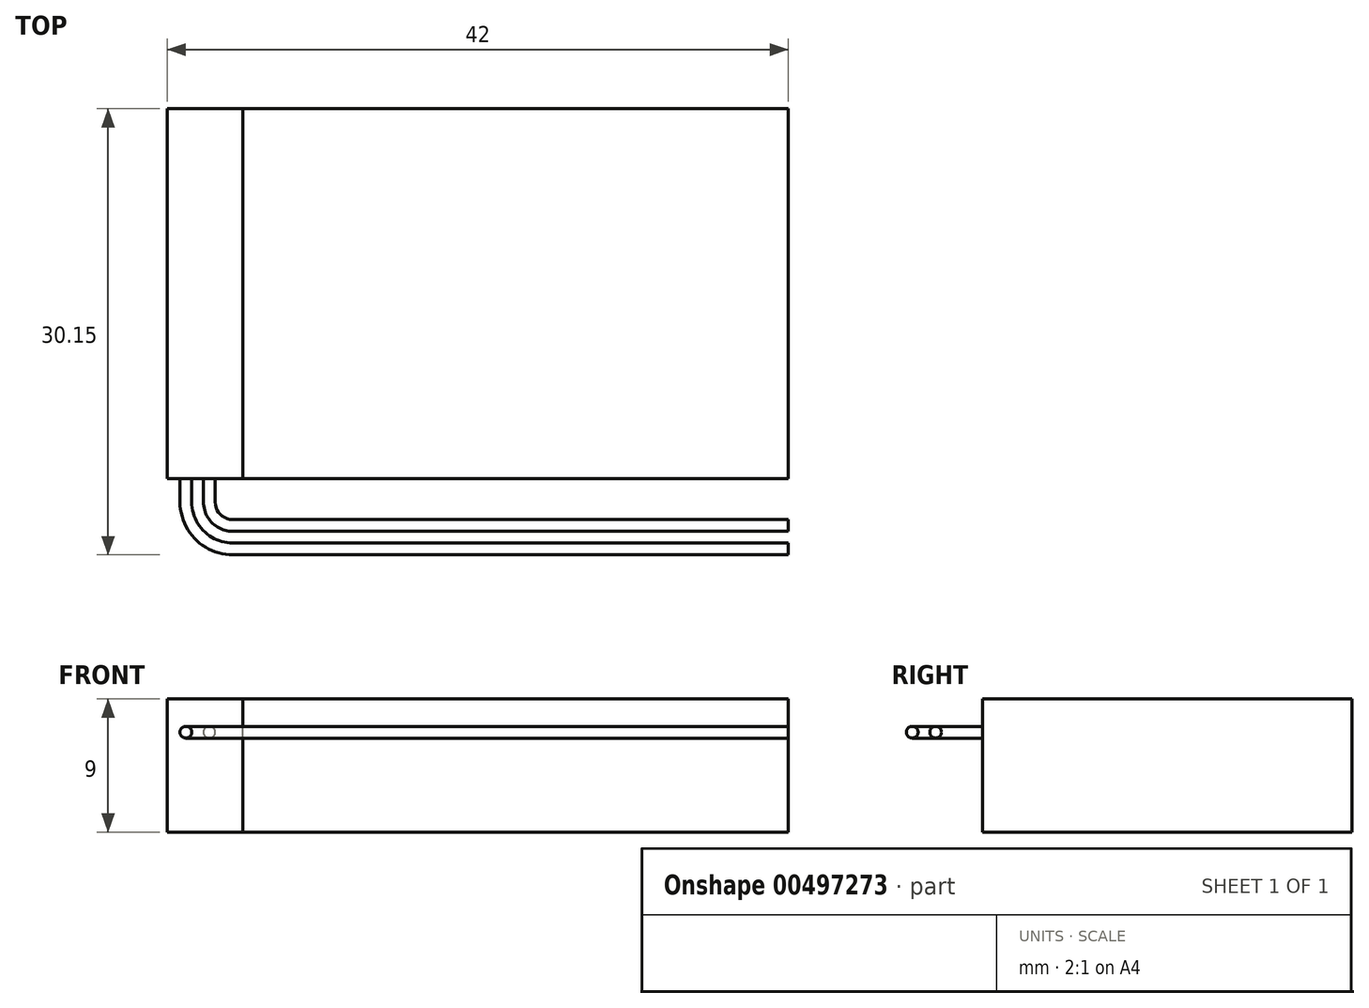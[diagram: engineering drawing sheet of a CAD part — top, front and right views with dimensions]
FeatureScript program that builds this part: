
annotation { "Feature Type Name" : "Feature", "Feature Type Description" : "" }
export const myFeature = defineFeature(function(context is Context, id is Id, definition is map)
    precondition{}
    {
        {
            var Q0;
            Q0=qCreatedBy(makeId("Top.planeOp"),FACE);
            var sketch = newSketch(context, id + "F0", { "sketchPlane" : qUnion([Q0])});
            skLineSegment(sketch, "E0.bottom", {"start": v(21, -12.5) * mm, "end": v(-21, -12.5) * mm});
            skLineSegment(sketch, "E0.top", {"start": v(21, 12.5) * mm, "end": v(-21, 12.5) * mm});
            skLineSegment(sketch, "E0.left", {"start": v(21, -12.5) * mm, "end": v(21, 12.5) * mm});
            skLineSegment(sketch, "E0.right", {"start": v(-21, -12.5) * mm, "end": v(-21, 12.5) * mm});
            skPoint(sketch, "E0.middle", {"position": v(0, 0) * mm});
            skSolve(sketch);
        }
        {
            var Q0;
            Q0=qSketchRegion(id+"F0",true);
            extrude(context, id + "F1", {"entities" : qUnion([Q0]), "depth" : 9 * mm});
        }
        {
            var Q0;
            Q0=makeQuery(id+"F1.opExtrude","CAP_FACE",FACE,{"disambiguationData":[OSD([sQuery(id+"F0.wireOp",EDGE,"E0.bottom"),sQuery(id+"F0.wireOp",EDGE,"E0.top"),sQuery(id+"F0.wireOp",EDGE,"E0.left"),sQuery(id+"F0.wireOp",EDGE,"E0.right")])],"isStart":false});
            var sketch = newSketch(context, id + "F2", { "sketchPlane" : qUnion([Q0])});
            skLineSegment(sketch, "E1.bottom", {"start": v(-21, 12.5) * mm, "end": v(-15.88, 12.5) * mm});
            skLineSegment(sketch, "E1.top", {"start": v(-21, -12.5) * mm, "end": v(-15.88, -12.5) * mm});
            skLineSegment(sketch, "E1.left", {"start": v(-21, 12.5) * mm, "end": v(-21, -12.5) * mm});
            skLineSegment(sketch, "E1.right", {"start": v(-15.88, 12.5) * mm, "end": v(-15.88, -12.5) * mm});
            skSolve(sketch);
        }
        {
            var Q0;
            Q0=makeQuery(id+"F2.imprint","IMPRINT",FACE,{"disambiguationData":[TD([[makeQuery(id+"F2.imprint","IMPRINT",EDGE,{"derivedFrom":sQuery(id+"F2.wireOp",EDGE,"E1.bottom")}),1.0]])]});
            extrude(context, id + "F3", {"entities" : qUnion([Q0]), "operationType" : NewBodyOperationType.REMOVE, "endBound" : BoundingType.THROUGH_ALL, "oppositeDirection" : true, "depth" : 9 * mm});
        }
        {
            var Q0;
            Q0=qSketchRegion(id+"F2",true);
            extrude(context, id + "F4", {"entities" : qUnion([Q0]), "oppositeDirection" : true, "depth" : 9 * mm});
        }
        {
            var Q0;
            Q0=qCreatedBy(makeId("Top.planeOp"),FACE);
            cPlane(context, id + "F5", {"entities" : qUnion([Q0]), "cplaneType" : CPlaneType.OFFSET, "offset" : .9 / 4 * 30 * mm, "width" : 152.4 * mm, "height" : 152.4 * mm});
        }
        {
            var Q0;
            Q0=makeQuery(id+"F4.opExtrude","SWEPT_FACE",FACE,{"disambiguationData":[OSD([sQuery(id+"F2.wireOp",EDGE,"E1.top")])]});
            var sketch = newSketch(context, id + "F6", { "sketchPlane" : qUnion([Q0])});
            skCircle(sketch, "E2", {"center": v(-19.74, 6.75) * mm, "radius": 0.4 * mm});
            skCircle(sketch, "E3", {"center": v(-18.15, 6.75) * mm, "radius": 0.4 * mm});
            skSolve(sketch);
        }
        {
            var Q0;
            Q0=qCreatedBy(id+"F5.planeOp",FACE);
            var sketch = newSketch(context, id + "F7", { "sketchPlane" : qUnion([Q0])});
            skLineSegment(sketch, "E4", {"start": v(-16.57, -15.68) * mm, "end": v(21, -15.68) * mm});
            skLineSegment(sketch, "E5", {"start": v(-16.57, -17.26) * mm, "end": v(21, -17.26) * mm});
            skLineSegment(sketch, "E6", {"start": v(-19.74, -14.09) * mm, "end": v(-19.74, -12.5) * mm});
            skLineSegment(sketch, "E7", {"start": v(-18.15, -14.09) * mm, "end": v(-18.15, -12.5) * mm});
            skArc(sketch, "E8", {"start": v(-18.15, -14.09) * mm, "mid": v(-17.69, -15.21) * mm, "end": v(-16.57, -15.68) * mm});
            skArc(sketch, "E9", {"start": v(-19.74, -14.09) * mm, "mid": v(-18.8, -16.33) * mm, "end": v(-16.57, -17.26) * mm});
            skSolve(sketch);
        }
        {
            var Q0;
            Q0=makeQuery(id+"F6.imprint","IMPRINT",FACE,{"disambiguationData":[TD([[makeQuery(id+"F6.imprint","IMPRINT",EDGE,{"derivedFrom":sQuery(id+"F6.wireOp",EDGE,"E3")}),1.0]])]});
            var Q1;
            Q1=sQuery(id+"F7.wireOp",EDGE,"E7");
            var Q2;
            Q2=sQuery(id+"F7.wireOp",EDGE,"E8");
            var Q3;
            Q3=sQuery(id+"F7.wireOp",EDGE,"E4");
            sweep(context, id + "F8", {"profiles" : qUnion([Q0]), "path" : qUnion([Q1, Q2, Q3])});
        }
        {
            var Q0;
            Q0=makeQuery(id+"F6.imprint","IMPRINT",FACE,{"disambiguationData":[TD([[makeQuery(id+"F6.imprint","IMPRINT",EDGE,{"derivedFrom":sQuery(id+"F6.wireOp",EDGE,"E2")}),1.0]])]});
            var Q1;
            Q1=sQuery(id+"F6.wireOp",EDGE,"E2");
            var Q2;
            Q2=sQuery(id+"F7.wireOp",EDGE,"E6");
            var Q3;
            Q3=sQuery(id+"F7.wireOp",EDGE,"E9");
            var Q4;
            Q4=sQuery(id+"F7.wireOp",EDGE,"E5");
            sweep(context, id + "F9", {"profiles" : qUnion([Q0]), "surfaceProfiles" : qUnion([Q1]), "path" : qUnion([Q2, Q3, Q4])});
        }
    });
